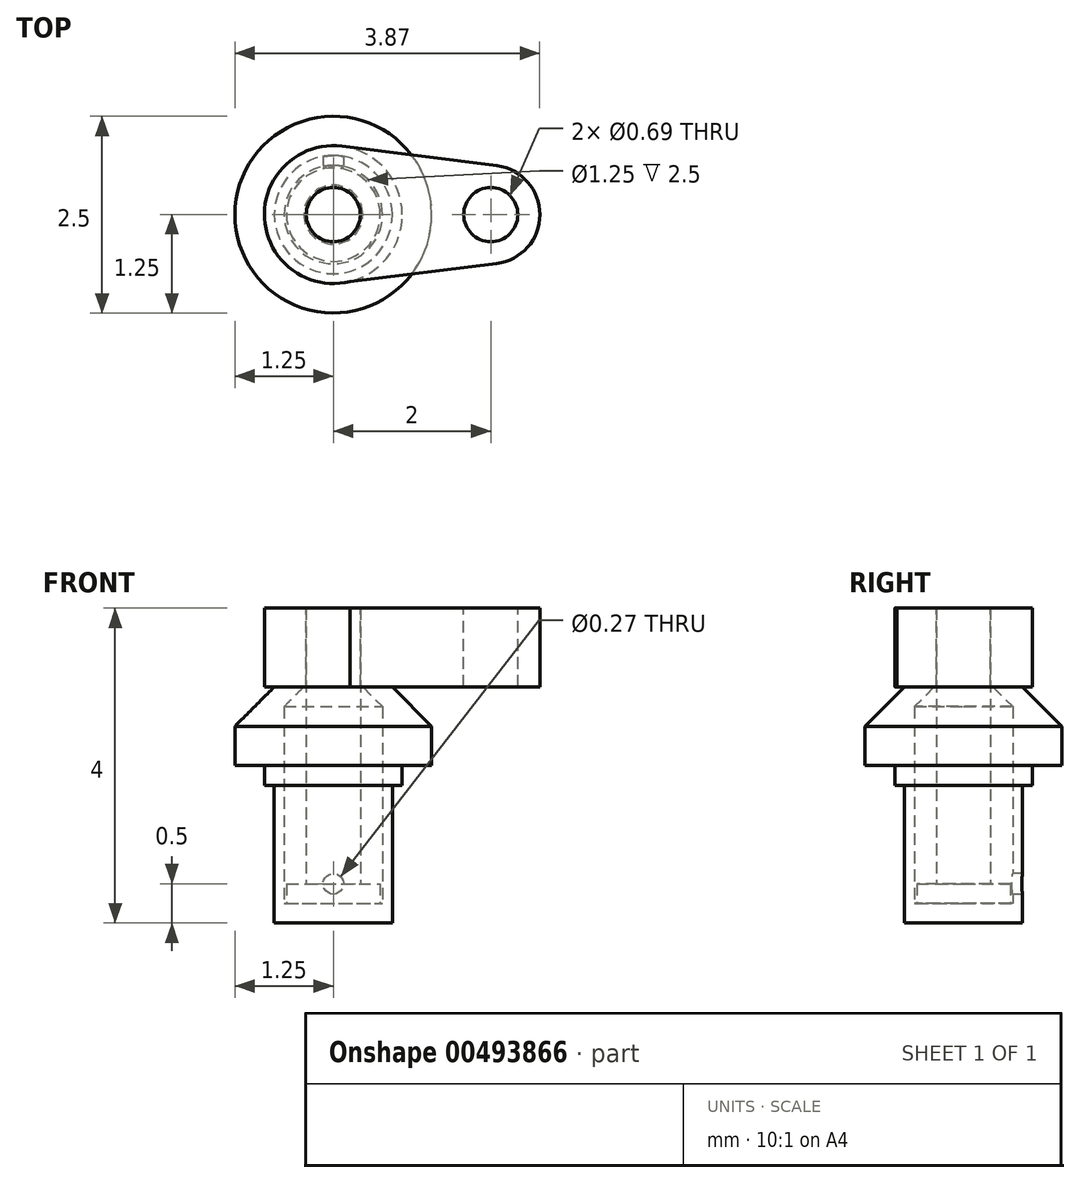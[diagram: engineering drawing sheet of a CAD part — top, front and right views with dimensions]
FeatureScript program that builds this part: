
annotation { "Feature Type Name" : "Feature", "Feature Type Description" : "" }
export const myFeature = defineFeature(function(context is Context, id is Id, definition is map)
    precondition{}
    {
        {
            var Q0;
            Q0=qCreatedBy(makeId("Front.planeOp"),FACE);
            var sketch = newSketch(context, id + "F0", { "sketchPlane" : qUnion([Q0])});
            skLineSegment(sketch, "E0", {"start": v(0, 0) * mm, "end": v(0, 3) * mm});
            skLineSegment(sketch, "E1", {"start": v(0, 3) * mm, "end": v(0.75, 3) * mm});
            skLineSegment(sketch, "E2", {"start": v(0.75, 3) * mm, "end": v(1.25, 2.5) * mm});
            skLineSegment(sketch, "E3", {"start": v(1.25, 2.5) * mm, "end": v(1.25, 2) * mm});
            skLineSegment(sketch, "E4", {"start": v(1.25, 2) * mm, "end": v(0.87, 2) * mm});
            skLineSegment(sketch, "E5", {"start": v(0.87, 2) * mm, "end": v(0.88, 1.75) * mm});
            skLineSegment(sketch, "E6", {"start": v(0.88, 1.75) * mm, "end": v(0.75, 1.75) * mm});
            skLineSegment(sketch, "E7", {"start": v(0.75, 1.75) * mm, "end": v(0.75, 0) * mm});
            skLineSegment(sketch, "E8", {"start": v(0.75, 0) * mm, "end": v(0, 0) * mm});
            skLineSegment(sketch, "E9", {"start": v(0.37, 3) * mm, "end": v(0.62, 2.75) * mm});
            skLineSegment(sketch, "E10", {"start": v(0.62, 2.75) * mm, "end": v(0.63, 0.25) * mm});
            skLineSegment(sketch, "E11", {"start": v(0.63, 0.25) * mm, "end": v(0, 0.25) * mm});
            skLineSegment(sketch, "E12", {"start": v(0, 0) * mm, "end": v(0, 3.36) * mm, "construction": true});
            skLineSegment(sketch, "E13", {"start": v(0.6, 0.25) * mm, "end": v(0.6, 0.5) * mm});
            skLineSegment(sketch, "E14", {"start": v(0.6, 0.5) * mm, "end": v(0.34, 0.5) * mm});
            skLineSegment(sketch, "E15", {"start": v(0.34, 0.5) * mm, "end": v(0.34, 4) * mm});
            skLineSegment(sketch, "E16", {"start": v(0.34, 4) * mm, "end": v(0, 4) * mm});
            skLineSegment(sketch, "E17", {"start": v(0, 4) * mm, "end": v(0, 3) * mm});
            skSolve(sketch);
        }
        {
            var Q0;
            {var subQ4=sQuery(id+"F0.wireOp",EDGE,"E2");Q0=makeQuery(id+"F0.imprint","IMPRINT",FACE,{"disambiguationData":[TD([[makeQuery(id+"F0.imprint","IMPRINT",EDGE,{"derivedFrom":subQ4}),-1.0]])]});}
            var Q1;
            Q1=sQuery(id+"F0.wireOp",EDGE,"E2");
            var Q2;
            Q2=sQuery(id+"F0.wireOp",EDGE,"E12");
            revolve(context, id + "F1", {"entities" : qUnion([Q0]), "surfaceEntities" : qUnion([Q1]), "axis" : qUnion([Q2]), "revolveType" : RevolveType.FULL});
        }
        {
            var Q0;
            {var subQ3=sQuery(id+"F0.wireOp",EDGE,"E13");Q0=makeQuery(id+"F0.imprint","IMPRINT",FACE,{"disambiguationData":[TD([[makeQuery(id+"F0.imprint","IMPRINT",EDGE,{"derivedFrom":subQ3}),1.0]])]});}
            var Q1;
            {var subQ4=sQuery(id+"F0.wireOp",EDGE,"E16");Q1=makeQuery(id+"F0.imprint","IMPRINT",FACE,{"disambiguationData":[TD([[makeQuery(id+"F0.imprint","IMPRINT",EDGE,{"derivedFrom":subQ4}),1.0]])]});}
            var Q2;
            Q2=sQuery(id+"F0.wireOp",EDGE,"E0");
            revolve(context, id + "F2", {"entities" : qUnion([Q0, Q1]), "axis" : qUnion([Q2]), "revolveType" : RevolveType.FULL});
        }
        {
            var Q0;
            Q0=makeQuery(id+"F2.opRevolve","SWEPT_FACE",FACE,{"disambiguationData":[OSD([sQuery(id+"F0.wireOp",EDGE,"E16")])]});
            var sketch = newSketch(context, id + "F3", { "sketchPlane" : qUnion([Q0])});
            skCircle(sketch, "E18.0", {"center": v(0, 0) * mm, "radius": 0.34 * mm});
            skCircle(sketch, "E19", {"center": v(0, 0) * mm, "radius": 0.88 * mm});
            skCircle(sketch, "E20", {"center": v(2, 0) * mm, "radius": 0.62 * mm});
            skCircle(sketch, "E21", {"center": v(2, 0) * mm, "radius": 0.34 * mm});
            skLineSegment(sketch, "E22", {"start": v(2.08, 0.62) * mm, "end": v(0.1, 0.87) * mm});
            skLineSegment(sketch, "E23", {"start": v(0, -0.88) * mm, "end": v(2.08, -0.62) * mm});
            skSolve(sketch);
        }
        {
            var Q0;
            Q0 = qSketchRegion(id + "F3", true);
            var Q1;
            Q1=makeQuery(id+"F1.opRevolve","SWEPT_FACE",FACE,{"disambiguationData":[OSD([sQuery(id+"F0.wireOp",EDGE,"E1")])]});
            extrude(context, id + "F4", {"entities" : qUnion([Q0]), "endBound" : BoundingType.UP_TO_SURFACE, "oppositeDirection" : true, "endBoundEntityFace" : qUnion([Q1]), "depth" : 1 * mm});
        }
        {
            var Q0;
            Q0=qCreatedBy(makeId("Front.planeOp"),FACE);
            var sketch = newSketch(context, id + "F5", { "sketchPlane" : qUnion([Q0])});
            skPoint(sketch, "E24", {"position": v(0, 0.5) * mm});
            skSolve(sketch);
        }
        {
            var Q0;
            Q0=sQuery(id+"F5.wireOp",VERTEX,"E24");
            var Q1;
            Q1=makeQuery(id+"F1.opRevolve","SWEPT_BODY",BODY,{"disambiguationData":[OSD([sQuery(id+"F0.wireOp",EDGE,"E0"),sQuery(id+"F0.wireOp",EDGE,"E1"),sQuery(id+"F0.wireOp",EDGE,"E2"),sQuery(id+"F0.wireOp",EDGE,"E3"),sQuery(id+"F0.wireOp",EDGE,"E4"),sQuery(id+"F0.wireOp",EDGE,"E5"),sQuery(id+"F0.wireOp",EDGE,"E6"),sQuery(id+"F0.wireOp",EDGE,"E7"),sQuery(id+"F0.wireOp",EDGE,"E8"),sQuery(id+"F0.wireOp",EDGE,"E9"),sQuery(id+"F0.wireOp",EDGE,"E10"),sQuery(id+"F0.wireOp",EDGE,"E11")])]});
            hole(context, id + "F6", {"style" : HoleStyle.SIMPLE, "endStyle" : HoleEndStyle.THROUGH, "holeDiameter" : .266 * mm, "isTappedThrough" : true, "tappedDepth" : 12 * mm, "tapClearance" : 3, "locations" : qUnion([Q0]), "scope" : qUnion([Q1])});
        }
    });
